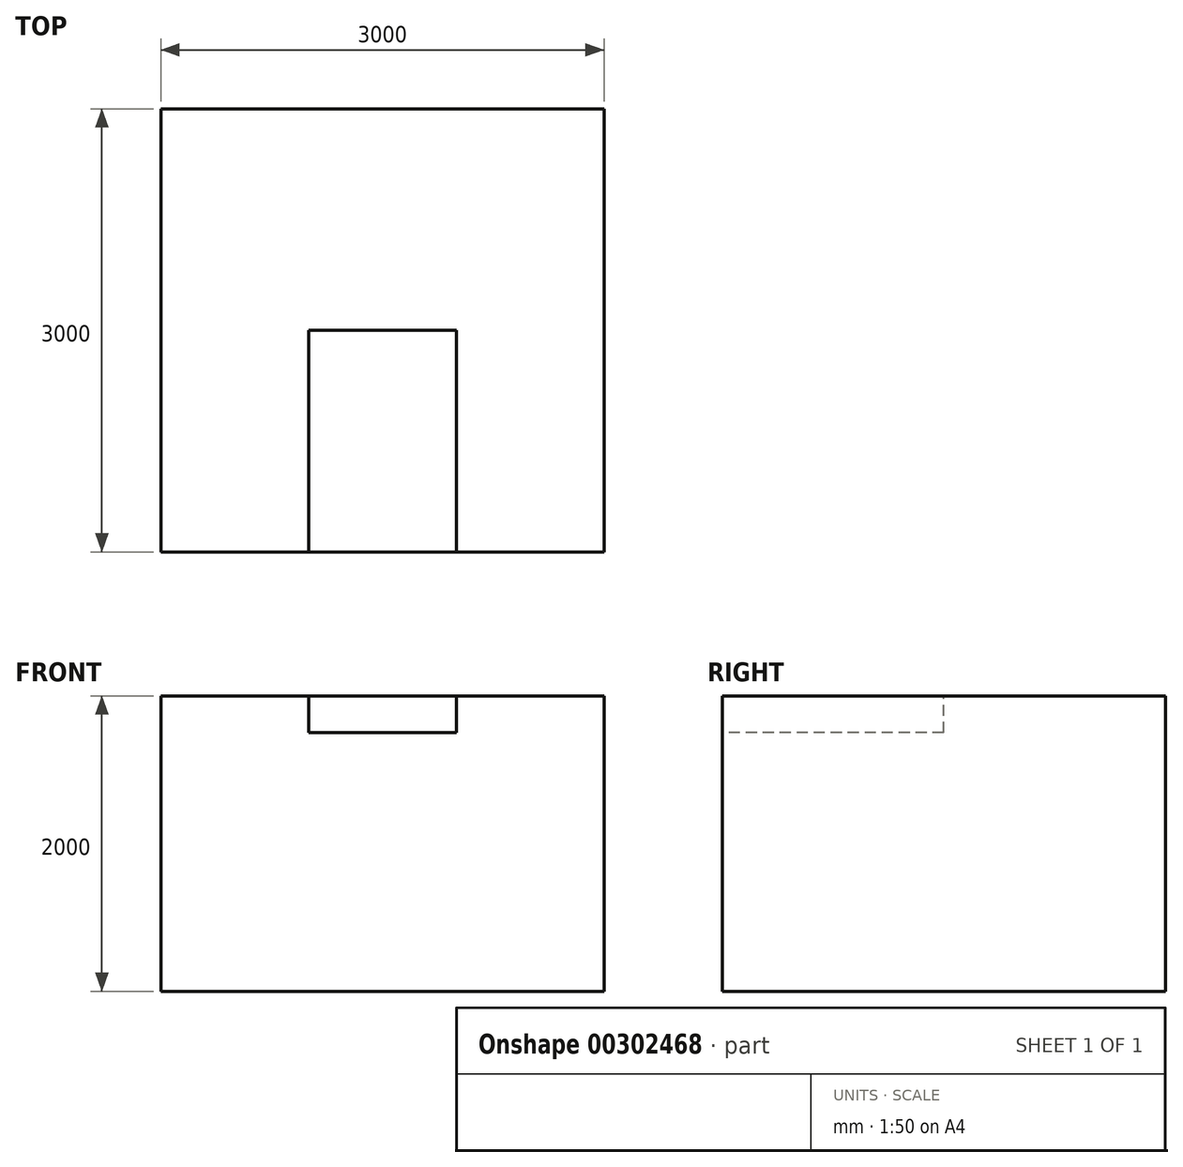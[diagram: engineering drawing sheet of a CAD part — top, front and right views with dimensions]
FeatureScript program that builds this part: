
annotation { "Feature Type Name" : "Feature", "Feature Type Description" : "" }
export const myFeature = defineFeature(function(context is Context, id is Id, definition is map)
    precondition{}
    {
        {
            var Q0;
            Q0=qCreatedBy(makeId("Front.planeOp"),FACE);
            var sketch = newSketch(context, id + "F0", { "sketchPlane" : qUnion([Q0])});
            skLineSegment(sketch, "E0.bottom", {"start": v(-1000, 250) * mm, "end": v(2000, 250) * mm});
            skLineSegment(sketch, "E0.top", {"start": v(-1000, -1750) * mm, "end": v(2000, -1750) * mm});
            skLineSegment(sketch, "E0.left", {"start": v(-1000, 250) * mm, "end": v(-1000, -1750) * mm});
            skLineSegment(sketch, "E0.right", {"start": v(2000, 250) * mm, "end": v(2000, -1750) * mm});
            skSolve(sketch);
        }
        {
            var Q0;
            Q0=makeQuery(id+"F0.imprint","IMPRINT",FACE,{"disambiguationData":[TD([[makeQuery(id+"F0.imprint","IMPRINT",EDGE,{"derivedFrom":sQuery(id+"F0.wireOp",EDGE,"E0.bottom")}),-1.0]])]});
            extrude(context, id + "F1", {"entities" : qUnion([Q0]), "oppositeDirection" : true, "depth" : 3000 * mm});
        }
        {
            var Q0;
            Q0=makeQuery(id+"F1.opExtrude","CAP_FACE",FACE,{"disambiguationData":[OSD([sQuery(id+"F0.wireOp",EDGE,"E0.bottom"),sQuery(id+"F0.wireOp",EDGE,"E0.top"),sQuery(id+"F0.wireOp",EDGE,"E0.left"),sQuery(id+"F0.wireOp",EDGE,"E0.right")])],"isStart":true});
            var sketch = newSketch(context, id + "F2", { "sketchPlane" : qUnion([Q0])});
            skLineSegment(sketch, "E1.bottom", {"start": v(0, 0) * mm, "end": v(1000, 0) * mm});
            skLineSegment(sketch, "E1.top", {"start": v(0, 250) * mm, "end": v(1000, 250) * mm});
            skLineSegment(sketch, "E1.left", {"start": v(0, 0) * mm, "end": v(0, 250) * mm});
            skLineSegment(sketch, "E1.right", {"start": v(1000, 0) * mm, "end": v(1000, 250) * mm});
            skSolve(sketch);
        }
        {
            var Q0;
            Q0 = qSketchRegion(id + "F2", true);
            extrude(context, id + "F3", {"entities" : qUnion([Q0]), "operationType" : NewBodyOperationType.REMOVE, "oppositeDirection" : true, "depth" : 1500 * mm});
        }
    });
